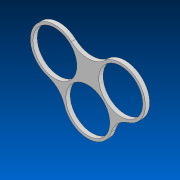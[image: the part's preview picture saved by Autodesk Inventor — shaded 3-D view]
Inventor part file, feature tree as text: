
AUTODESK INVENTOR PART (.ipt)
format: ipt  version: 2022 (Build 260153000, 153)  size: 106,496 bytes
history: native  units: in
note: dims shown in document units (in); Inventor stores cm internally (conversion verified against a paired STEP export)
features: extrude x1, sketch x1
ambient origin geometry x8: Origin, YZ Plane, XZ Plane, XY Plane, X Axis, Y Axis, Z Axis, Center Point
bodies: Solid1 (feature_tree)
feature tree (2):
  extrude  "Extrusion1"  Depth=0.25in
  sketch  "Sketch1"  dims[d0=5.4in d1=2.55in d2=0.25in d3=0.0in]
